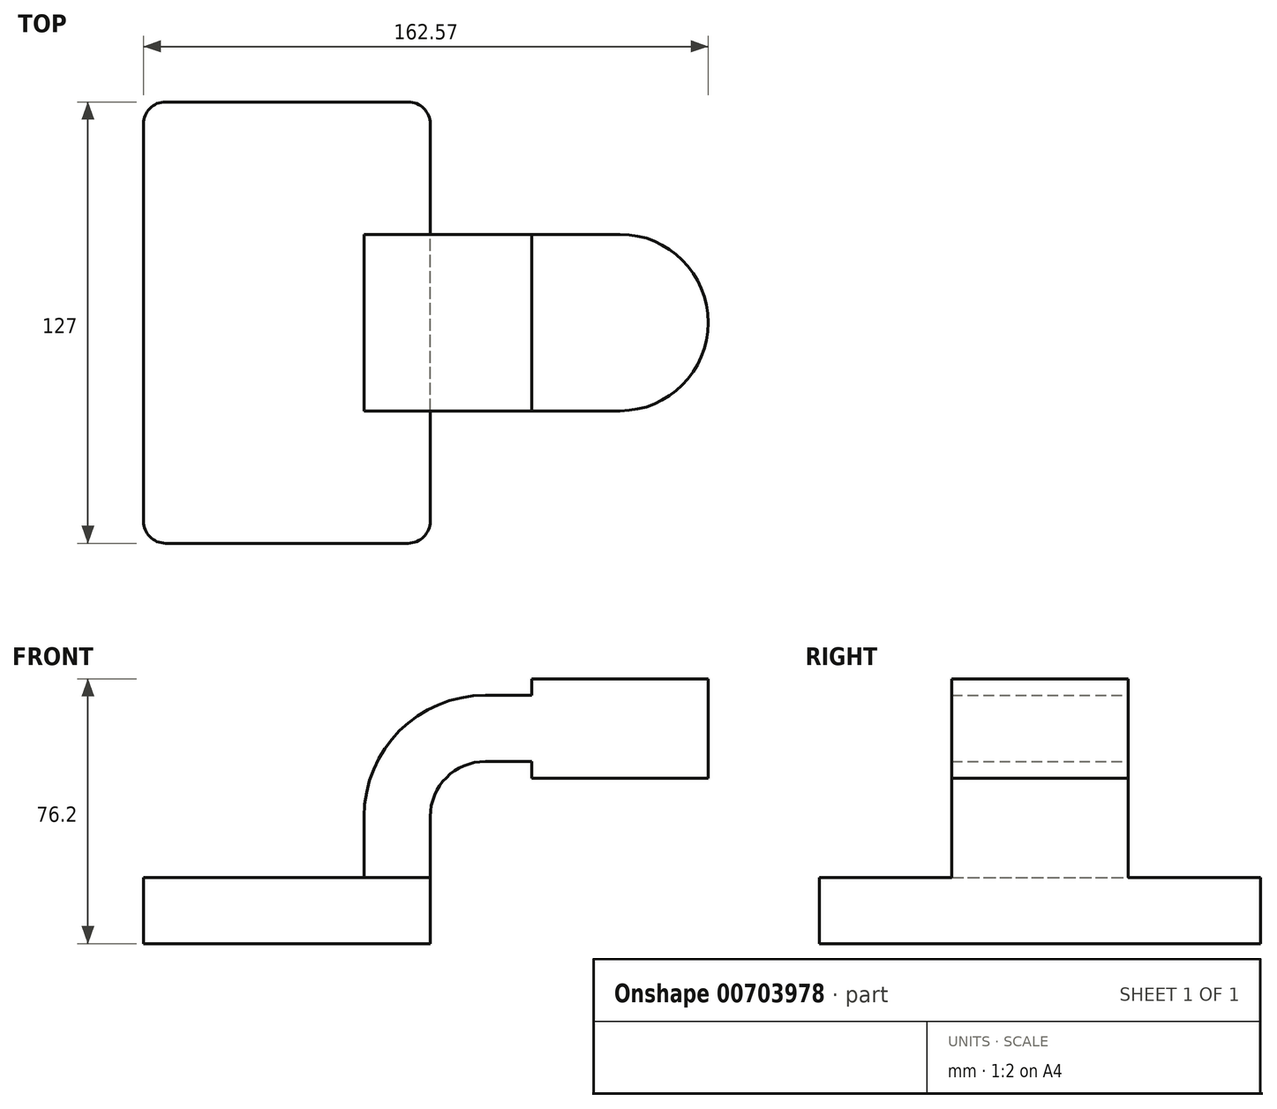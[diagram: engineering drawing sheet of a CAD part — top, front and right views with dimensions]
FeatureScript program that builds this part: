
annotation { "Feature Type Name" : "Feature", "Feature Type Description" : "" }
export const myFeature = defineFeature(function(context is Context, id is Id, definition is map)
    precondition{}
    {
        {
            var Q0;
            Q0=qCreatedBy(makeId("Front.planeOp"),FACE);
            var sketch = newSketch(context, id + "F0", { "sketchPlane" : qUnion([Q0])});
            skLineSegment(sketch, "E0.bottom", {"start": v(-41.28, 9.52) * mm, "end": v(41.28, 9.53) * mm});
            skLineSegment(sketch, "E0.top", {"start": v(-41.28, -9.53) * mm, "end": v(41.28, -9.53) * mm});
            skLineSegment(sketch, "E0.left", {"start": v(-41.28, 9.52) * mm, "end": v(-41.28, -9.53) * mm});
            skLineSegment(sketch, "E0.right", {"start": v(41.28, 9.53) * mm, "end": v(41.28, -9.52) * mm});
            skPoint(sketch, "E0.middle", {"position": v(0, 0) * mm});
            skLineSegment(sketch, "E1.bottom", {"start": v(70.5, 66.67) * mm, "end": v(121.3, 66.67) * mm});
            skLineSegment(sketch, "E1.top", {"start": v(70.5, 38.1) * mm, "end": v(121.3, 38.1) * mm});
            skLineSegment(sketch, "E1.left", {"start": v(70.5, 66.67) * mm, "end": v(70.5, 38.1) * mm});
            skLineSegment(sketch, "E1.right", {"start": v(121.3, 66.67) * mm, "end": v(121.3, 38.1) * mm});
            skPoint(sketch, "E1.middle", {"position": v(95.9, 52.39) * mm});
            skLineSegment(sketch, "E2", {"start": v(41.27, 9.53) * mm, "end": v(41.27, 27) * mm});
            skArc(sketch, "E3", {"start": v(41.27, 27) * mm, "mid": v(45.92, 38.23) * mm, "end": v(57.15, 42.88) * mm});
            skLineSegment(sketch, "E4", {"start": v(57.15, 42.88) * mm, "end": v(87.92, 42.88) * mm});
            skLineSegment(sketch, "E5.0", {"start": v(57.15, 61.93) * mm, "end": v(87.92, 61.93) * mm});
            skArc(sketch, "E5.1", {"start": v(22.22, 27) * mm, "mid": v(32.45, 51.7) * mm, "end": v(57.15, 61.93) * mm});
            skLineSegment(sketch, "E5.2", {"start": v(22.22, 9.53) * mm, "end": v(22.22, 27) * mm});
            skLineSegment(sketch, "E6", {"start": v(95.9, 38.1) * mm, "end": v(95.9, 66.67) * mm});
            skFitSpline(sketch, "E7", {"points": [v(-41.28, 9.52) * mm, v(57.15, 61.93) * mm], "startDerivative": vector(14.52, 84.46) * mm, "endDerivative": vector(222.2, -14.46) * mm});
            skSolve(sketch);
        }
        {
            var Q0;
            Q0=makeQuery(id+"F0.imprint","IMPRINT",FACE,{"disambiguationData":[TD([[makeQuery(id+"F0.imprint","IMPRINT",EDGE,{"derivedFrom":sQuery(id+"F0.wireOp",EDGE,"E0.top")}),1.0]])]});
            extrude(context, id + "F1", {"entities" : qUnion([Q0]), "endBound" : BoundingType.SYMMETRIC, "depth" : 127 * mm, "offsetDistance" : 25.4 * mm});
        }
        {
            var Q0;
            {var subQ1=sQuery(id+"F0.wireOp",EDGE,"E2");Q0=makeQuery(id+"F0.imprint","IMPRINT",FACE,{"disambiguationData":[TD([[makeQuery(id+"F0.imprint","IMPRINT",EDGE,{"derivedFrom":subQ1}),1.0]])]});}
            var Q1;
            {var subQ6=sQuery(id+"F0.wireOp",EDGE,"E6");Q1=makeQuery(id+"F0.imprint","IMPRINT",FACE,{"disambiguationData":[TD([[makeQuery(id+"F0.imprint","IMPRINT",EDGE,{"derivedFrom":subQ6}),1.0]])]});}
            extrude(context, id + "F2", {"entities" : qUnion([Q0, Q1]), "operationType" : NewBodyOperationType.ADD, "endBound" : BoundingType.SYMMETRIC, "depth" : 50.8 * mm, "offsetDistance" : 25.4 * mm});
        }
        {
            var Q0;
            Q0=makeQuery(id+"F0.imprint","IMPRINT",FACE,{"disambiguationData":[TD([[makeQuery(id+"F0.imprint","IMPRINT",EDGE,{"derivedFrom":sQuery(id+"F0.wireOp",EDGE,"E5.1")}),1.0]])]});
            extrude(context, id + "F3", {"entities" : qUnion([Q0]), "operationType" : NewBodyOperationType.ADD, "endBound" : BoundingType.SYMMETRIC, "depth" : 15.88 * mm, "offsetDistance" : 25.4 * mm});
        }
        {
            var Q0;
            {var subQ0=sQuery(id+"F0.wireOp",EDGE,"E1.right");Q0=makeQuery(id+"F0.imprint","IMPRINT",FACE,{"disambiguationData":[TD([[makeQuery(id+"F0.imprint","IMPRINT",EDGE,{"derivedFrom":subQ0}),-1.0]])]});}
            var Q1;
            Q1=sQuery(id+"F0.wireOp",EDGE,"E6");
            revolve(context, id + "F4", {"operationType" : NewBodyOperationType.ADD, "entities" : qUnion([Q0]), "axis" : qUnion([Q1]), "revolveType" : RevolveType.FULL});
        }
        {
            var Q0;
            Q0=makeQuery(id+"F1.opExtrude","CAP_EDGE",EDGE,{"disambiguationData":[OSD([sQuery(id+"F0.wireOp",EDGE,"E0.right")])],"isStart":false});
            var Q1;
            Q1=makeQuery(id+"F1.opExtrude","CAP_EDGE",EDGE,{"disambiguationData":[OSD([sQuery(id+"F0.wireOp",EDGE,"E0.left")])],"isStart":false});
            var Q2;
            Q2=makeQuery(id+"F1.opExtrude","CAP_EDGE",EDGE,{"disambiguationData":[OSD([sQuery(id+"F0.wireOp",EDGE,"E0.right")])],"isStart":true});
            var Q3;
            Q3=makeQuery(id+"F1.opExtrude","CAP_EDGE",EDGE,{"disambiguationData":[OSD([sQuery(id+"F0.wireOp",EDGE,"E0.left")])],"isStart":true});
            fillet(context, id + "F5", {"entities" : qUnion([Q0, Q1, Q2, Q3]), "radius" : 6.35 * mm, "tangentPropagation" : true, "allowEdgeOverflow" : false});
        }
    });
